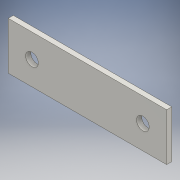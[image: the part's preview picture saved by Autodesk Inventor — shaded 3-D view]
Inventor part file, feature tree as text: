
AUTODESK INVENTOR PART (.ipt)
format: ipt  version: 2018 (Build 220112000, 112)  size: 104,448 bytes
history: native  units: mm
features: extrude x2, sketch x2
ambient origin geometry x8: Origin, YZ Plane, XZ Plane, XY Plane, X Axis, Y Axis, Z Axis, Center Point
bodies: Solid1 (feature_tree)
feature tree (4):
  extrude  "Extrusion1"  Depth=15.0mm
  extrude  "Extrusion2"  Depth=10.0mm
  sketch  "Sketch1"  dims[d0=50.0mm d1=15.0mm]
  sketch  "Sketch2"  dims[d2=1.6mm d3=0.0mm d4=4.0mm d5=7.5mm d6=4.0mm d7=7.5mm d8=10.0mm d9=0.0mm]
